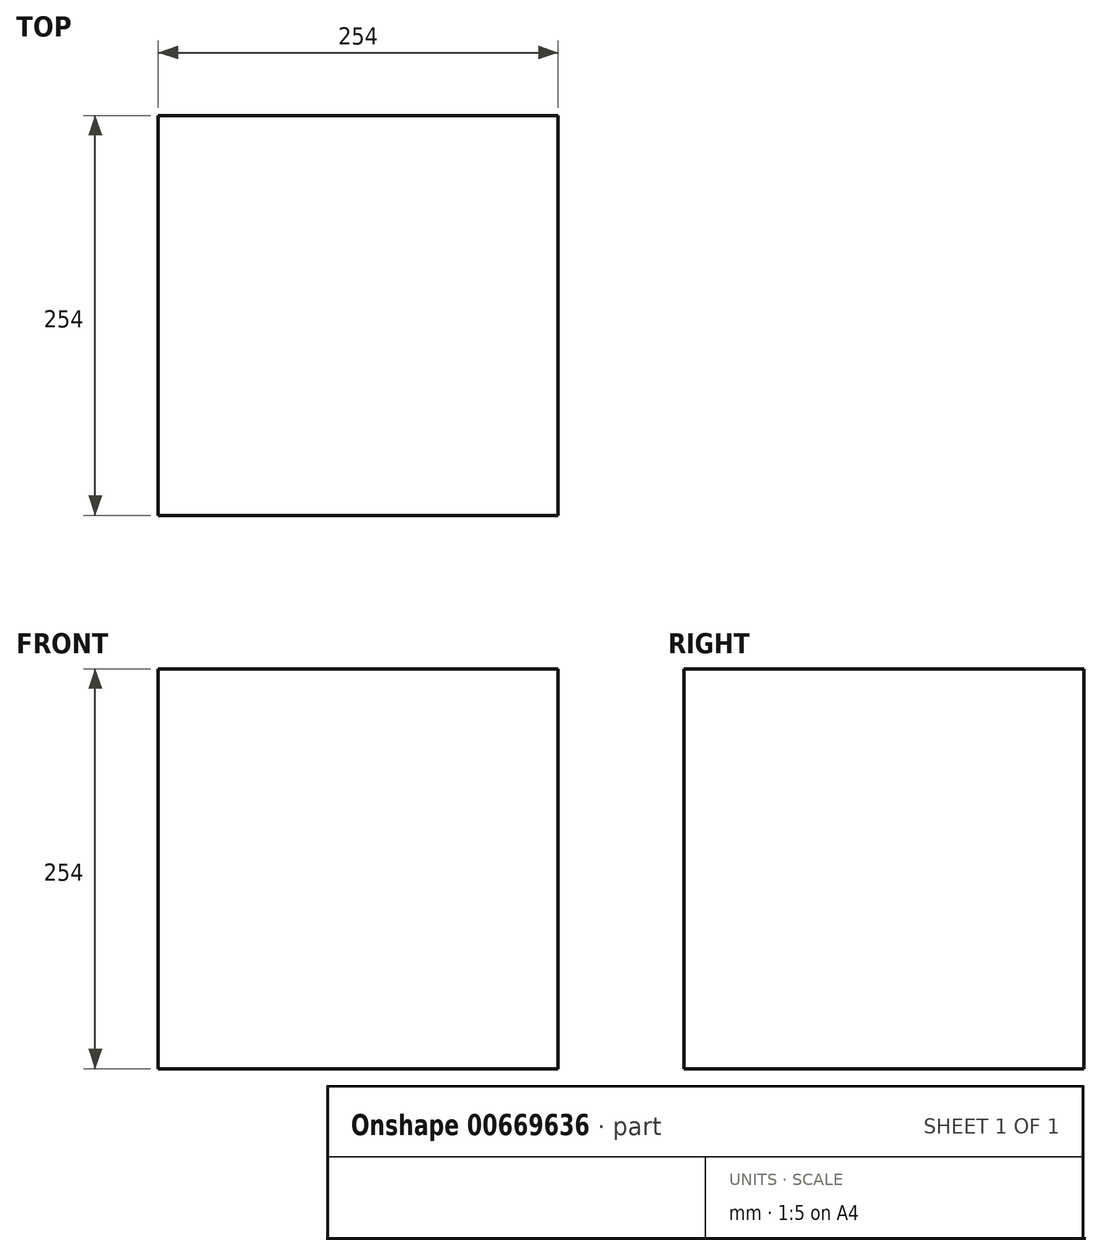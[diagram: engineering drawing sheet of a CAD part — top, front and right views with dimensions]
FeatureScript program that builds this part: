
annotation { "Feature Type Name" : "Feature", "Feature Type Description" : "" }
export const myFeature = defineFeature(function(context is Context, id is Id, definition is map)
    precondition{}
    {
        {
            var Q0;
            Q0=qCreatedBy(makeId("Front.planeOp"),FACE);
            var sketch = newSketch(context, id + "F0", { "sketchPlane" : qUnion([Q0])});
            skLineSegment(sketch, "E0", {"start": v(0, 254) * mm, "end": v(0, 0) * mm});
            skLineSegment(sketch, "E1", {"start": v(0, 0) * mm, "end": v(254, 0) * mm});
            skLineSegment(sketch, "E2", {"start": v(254, 0) * mm, "end": v(254, 254) * mm});
            skLineSegment(sketch, "E3", {"start": v(254, 254) * mm, "end": v(0, 254) * mm});
            skSolve(sketch);
        }
        {
            var Q0;
            Q0 = qSketchRegion(id + "F0", true);
            extrude(context, id + "F1", {"entities" : qUnion([Q0]), "depth" : 254 * mm, "offsetDistance" : 25.4 * mm});
        }
    });
